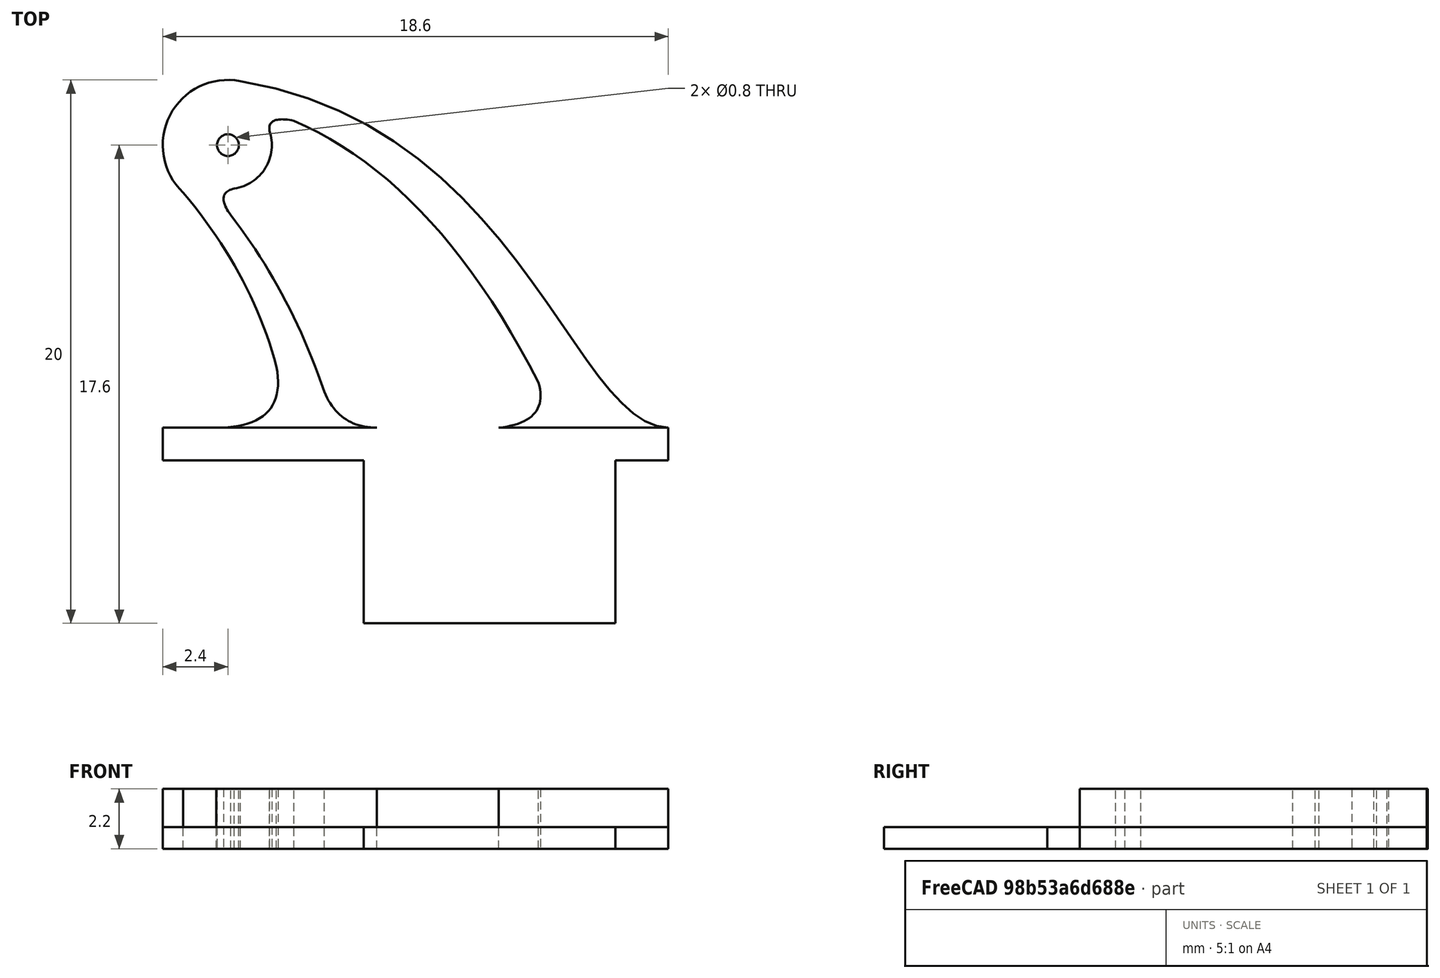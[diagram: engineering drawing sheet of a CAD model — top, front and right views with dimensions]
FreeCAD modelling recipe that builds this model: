
FCSTD DOCUMENT  (FreeCAD 0.20R0.20.2)
Label: 009
License: All rights reserved
LicenseURL: http://en.wikipedia.org/wiki/All_rights_reserved
objects: Sketcher::SketchObject×3, Part::Extrusion×2
note: 5 computed .brp shape members not serialized (recipe doc carries the construction recipe); baked Part::Feature solids carry a one-line shape summary decoded from their .brp

FEATURE [Sketcher::SketchObject] Sketch  label="main"
  FullyConstrained = true
  sketch-geometry (25):
    g0: LineSegment StartX=12.0586 StartY=-6 StartZ=0 EndX=12.0586 EndY=0 EndZ=0
    g1: LineSegment StartX=2.8 StartY=-6 StartZ=0 EndX=2.8 EndY=0 EndZ=0
    g2: LineSegment StartX=2.8 StartY=-6 StartZ=0 EndX=12.0586 EndY=-6 EndZ=0
    g3: LineSegment StartX=12.0586 StartY=0 StartZ=0 EndX=14 EndY=0 EndZ=0
    g4: LineSegment StartX=2.8 StartY=0 StartZ=0 EndX=0 EndY=0 EndZ=0
    g5: LineSegment StartX=14 StartY=0 StartZ=0 EndX=14 EndY=1.2 EndZ=0
    g6: LineSegment StartX=0 StartY=0 StartZ=0 EndX=-4.6 EndY=0 EndZ=0
    g7: Circle CenterX=-2.2 CenterY=11.6 CenterZ=0 NormalX=0 NormalY=0 NormalZ=1 AngleXU=0 Radius=0.4
    g8-g11: Circle x4 (B-spline internal-alignment scaffolding for g12; pole/knot coordinates omitted)
    g12: BSplineCurve PolesCount=4 KnotsCount=2 Degree=3 IsPeriodic=0
    g13: GeomPoint X=-1.74436 Y=13.9564 Z=0
    g14: GeomPoint X=14 Y=1.2 Z=0
    g15: ArcOfCircle CenterX=-2.2 CenterY=11.6 CenterZ=0 NormalX=0 NormalY=0 NormalZ=1 AngleXU=0 Radius=2.4 StartAngle=1.37979 EndAngle=3.95565
    g16: LineSegment StartX=-2.62672 StartY=1.2 StartZ=0 EndX=-4.6 EndY=1.2 EndZ=0
    g17: LineSegment StartX=-4.6 StartY=0 StartZ=0 EndX=-4.6 EndY=1.2 EndZ=0
    g18: Circle CenterX=-2.62672 CenterY=1.2 CenterZ=0 NormalX=0 NormalY=0 NormalZ=1 AngleXU=0 Radius=1
    g19: Circle CenterX=0 CenterY=1.2 CenterZ=0 NormalX=0 NormalY=0 NormalZ=1 AngleXU=0 Radius=1
    g20: Circle CenterX=-0.413885 CenterY=3.44541 CenterZ=0 NormalX=0 NormalY=0 NormalZ=1 AngleXU=0 Radius=1
    g21: BSplineCurve PolesCount=3 KnotsCount=2 Degree=2 IsPeriodic=0
    g22: GeomPoint X=-2.62672 Y=1.2 Z=0
    g23: GeomPoint X=-0.413885 Y=3.44541 Z=0
    g24: BSplineCurve PolesCount=3 KnotsCount=2 Degree=2 IsPeriodic=0
  constraints (52):
    c: Vertical(g0)
    c: Vertical(g1)
    c: Block(g1)
    c: Block(g0)
    c: Distance(g1) = 6
    c: Coincident(g2,g1)
    c: Horizontal(g2)
    c: Coincident(g0,g2)
    c: Block(g2)
    c: Coincident(g3,g0)
    c: Horizontal(g3)
    c: Coincident(g4,g1)
    c: Horizontal(g4)
    c: Block(g3)
    c: Block(g4)
    c: Coincident(g5,g3)
    c: Vertical(g5)
    c: Distance(g5) = 1.2
    c: Coincident(g6,g4)
    c: Horizontal(g6)
    c: Distance(g6) = 4.6
    c: Block(g7)
    c: Weight(g8) = 1
    c: Equal(g8,g9)
    c: Equal(g8,g10)
    c: Equal(g8,g11)
    c: Coincident(g12,g5)
    c: InternalAlignment(g8-g11 -> g12) x4
    c: InternalAlignment(g13,g12)
    c: InternalAlignment(g14,g12)
    c: Block(g12)
    c: Coincident(g15,g7)
    c: Coincident(g15,g12)
    c: Coincident(g15,g24)
    c: Block(g15)
    c: Horizontal(g16)
    c: Coincident(g17,g6)
    c: Vertical(g17)
    c: Coincident(g17,g16)
    c: Weight(g18) = 1
    c: Equal(g18,g19)
    c: Equal(g18,g20)
    c: InternalAlignment(g18,g21)
    c: InternalAlignment(g19,g21)
    c: InternalAlignment(g20,g21)
    c: InternalAlignment(g22,g21)
    c: InternalAlignment(g23,g21)
    c: Block(g16)
    c: Coincident(g16,g21)
    c: Coincident(g21,g24)
    c: Block(g24)
    c: Block(g21)
FEATURE [Part::Extrusion] Extrude
  Base = -> Sketch
  Dir = (0,0,1)
  DirMode = 2
  FaceMakerClass = Part::FaceMakerBullseye
  LengthFwd = 0.8
  LengthRev = 0
  Solid = true
  Symmetric = false
FEATURE [Sketcher::SketchObject] Sketch001  label="main001"
  FullyConstrained = false
  sketch-geometry (45):
    g0: Circle CenterX=-2.2 CenterY=11.6 CenterZ=0 NormalX=0 NormalY=0 NormalZ=1 AngleXU=0 Radius=0.4
    g1-g4: Circle x4 (B-spline internal-alignment scaffolding for g5; pole/knot coordinates omitted)
    g5: BSplineCurve PolesCount=4 KnotsCount=2 Degree=3 IsPeriodic=0
    g6: GeomPoint X=-1.74436 Y=13.9564 Z=0
    g7: GeomPoint X=14 Y=1.2 Z=0
    g8: ArcOfCircle CenterX=-2.2 CenterY=11.6 CenterZ=0 NormalX=0 NormalY=0 NormalZ=1 AngleXU=0 Radius=2.4 StartAngle=1.37979 EndAngle=3.95565
    g9: Circle CenterX=-2.62672 CenterY=1.2 CenterZ=0 NormalX=0 NormalY=0 NormalZ=1 AngleXU=0 Radius=1
    g10: Circle CenterX=0 CenterY=1.2 CenterZ=0 NormalX=0 NormalY=0 NormalZ=1 AngleXU=0 Radius=1
    g11: Circle CenterX=-0.413885 CenterY=3.44541 CenterZ=0 NormalX=0 NormalY=0 NormalZ=1 AngleXU=0 Radius=1
    g12: BSplineCurve PolesCount=3 KnotsCount=2 Degree=2 IsPeriodic=0
    g13: GeomPoint X=-2.62672 Y=1.2 Z=0
    g14: GeomPoint X=-0.413885 Y=3.44541 Z=0
    g15: BSplineCurve PolesCount=3 KnotsCount=2 Degree=2 IsPeriodic=0
    g16: Circle CenterX=1.34801 CenterY=2.51783 CenterZ=0 NormalX=0 NormalY=0 NormalZ=1 AngleXU=0 Radius=1
    g17: Circle CenterX=1.8831 CenterY=1.2 CenterZ=0 NormalX=0 NormalY=0 NormalZ=1 AngleXU=0 Radius=1
    g18: Circle CenterX=3.28198 CenterY=1.2 CenterZ=0 NormalX=0 NormalY=0 NormalZ=1 AngleXU=0 Radius=1
    g19: BSplineCurve PolesCount=3 KnotsCount=2 Degree=2 IsPeriodic=0
    g20: GeomPoint X=1.34801 Y=2.51783 Z=0
    g21: GeomPoint X=3.28198 Y=1.2 Z=0
    g22: Circle CenterX=9.22372 CenterY=2.86164 CenterZ=0 NormalX=0 NormalY=0 NormalZ=1 AngleXU=0 Radius=1
    g23: Circle CenterX=9.64409 CenterY=1.39848 CenterZ=0 NormalX=0 NormalY=0 NormalZ=1 AngleXU=0 Radius=1
    g24: Circle CenterX=7.76214 CenterY=1.2 CenterZ=0 NormalX=0 NormalY=0 NormalZ=1 AngleXU=0 Radius=1
    g25: BSplineCurve PolesCount=3 KnotsCount=2 Degree=2 IsPeriodic=0
    g26: GeomPoint X=9.22372 Y=2.86164 Z=0
    g27: GeomPoint X=7.76214 Y=1.2 Z=0
    g28: LineSegment StartX=-2.62672 StartY=1.2 StartZ=0 EndX=3.28198 EndY=1.2 EndZ=0
    g29: LineSegment StartX=7.76214 StartY=1.2 StartZ=0 EndX=14 EndY=1.2 EndZ=0
    g30: Circle CenterX=-0.671756 CenterY=12.1251 CenterZ=0 NormalX=0 NormalY=0 NormalZ=1 AngleXU=0 Radius=1
    g31: Circle CenterX=-0.754831 CenterY=12.699 CenterZ=0 NormalX=0 NormalY=0 NormalZ=1 AngleXU=0 Radius=1
    g32: Circle CenterX=0.224587 CenterY=12.4971 CenterZ=0 NormalX=0 NormalY=0 NormalZ=1 AngleXU=0 Radius=1
    g33: BSplineCurve PolesCount=3 KnotsCount=2 Degree=2 IsPeriodic=0
    g34: GeomPoint X=-0.671756 Y=12.1251 Z=0
    g35: GeomPoint X=0.224587 Y=12.4971 Z=0
    g36: Circle CenterX=-2.10085 CenterY=9.02995 CenterZ=0 NormalX=0 NormalY=0 NormalZ=1 AngleXU=0 Radius=1
    g37: Circle CenterX=-2.68572 CenterY=9.84108 CenterZ=0 NormalX=0 NormalY=0 NormalZ=1 AngleXU=0 Radius=1
    g38: Circle CenterX=-1.96262 CenterY=10.0016 CenterZ=0 NormalX=0 NormalY=0 NormalZ=1 AngleXU=0 Radius=1
    g39: BSplineCurve PolesCount=3 KnotsCount=2 Degree=2 IsPeriodic=0
    g40: GeomPoint X=-2.10085 Y=9.02995 Z=0
    g41: GeomPoint X=-1.96262 Y=10.0016 Z=0
    g42: ArcOfCircle CenterX=-2.2 CenterY=11.6 CenterZ=0 NormalX=0 NormalY=0 NormalZ=1 AngleXU=0 Radius=1.61593 StartAngle=4.85982 EndAngle=6.61413
    g43: BSplineCurve PolesCount=3 KnotsCount=2 Degree=2 IsPeriodic=0
    g44: BSplineCurve PolesCount=3 KnotsCount=2 Degree=2 IsPeriodic=0
  constraints (76):
    c: Block(g0)
    c: Weight(g1) = 1
    c: Equal(g1,g2)
    c: Equal(g1,g3)
    c: Equal(g1,g4)
    c: InternalAlignment(g1-g4 -> g5) x4
    c: InternalAlignment(g6,g5)
    c: InternalAlignment(g7,g5)
    c: Block(g5)
    c: Coincident(g8,g0)
    c: Coincident(g8,g5)
    c: Coincident(g8,g15)
    c: Block(g8)
    c: Weight(g9) = 1
    c: Equal(g9,g11)
    c: InternalAlignment(g9,g12)
    c: InternalAlignment(g10,g12)
    c: InternalAlignment(g11,g12)
    c: InternalAlignment(g13,g12)
    c: InternalAlignment(g14,g12)
    c: Coincident(g12,g15)
    c: Block(g15)
    c: Block(g12)
    c: Weight(g16) = 1
    c: Equal(g16,g17)
    c: Equal(g16,g18)
    c: InternalAlignment(g16,g19)
    c: InternalAlignment(g17,g19)
    c: InternalAlignment(g18,g19)
    c: InternalAlignment(g20,g19)
    c: InternalAlignment(g21,g19)
    c: Block(g19)
    c: Weight(g22) = 1
    c: Coincident(g25,g43)
    c: Equal(g22,g23)
    c: Equal(g22,g24)
    c: InternalAlignment(g22,g25)
    c: InternalAlignment(g23,g25)
    c: InternalAlignment(g24,g25)
    c: InternalAlignment(g26,g25)
    c: InternalAlignment(g27,g25)
    c: Block(g25)
    c: Coincident(g28,g19)
    c: Horizontal(g28)
    c: Coincident(g29,g25)
    c: Horizontal(g29)
    c: Weight(g30) = 1
    c: Equal(g30,g31)
    c: Equal(g30,g32)
    c: InternalAlignment(g30,g33)
    c: InternalAlignment(g31,g33)
    c: InternalAlignment(g32,g33)
    c: InternalAlignment(g34,g33)
    c: InternalAlignment(g35,g33)
    c: Weight(g36) = 1
    c: Equal(g36,g37)
    c: Equal(g36,g38)
    c: InternalAlignment(g36,g39)
    c: InternalAlignment(g37,g39)
    c: InternalAlignment(g38,g39)
    c: InternalAlignment(g40,g39)
    c: InternalAlignment(g41,g39)
    c: Coincident(g42,g0)
    c: Coincident(g42,g39)
    c: Coincident(g42,g33)
    c: Block(g42)
    c: PointOnObject(g43,g31)
    c: PointOnObject(g44,g37)
    c: Coincident(g33,g43)
    c: Coincident(g39,g44)
    c: Block(g43)
    c: Block(g44)
    c: Block(g39)
    c: Block(g33)
    c: Block(g29)
    c: Block(g28)
FEATURE [Part::Extrusion] Extrude001
  Base = -> Sketch001
  Dir = (0,0,1)
  DirMode = 2
  FaceMakerClass = Part::FaceMakerBullseye
  LengthFwd = 2.2
  LengthRev = 0
  Solid = true
  Symmetric = false
FEATURE [Sketcher::SketchObject] Sketch002
  FullyConstrained = true
  Placement = pos=(0,0,0) rot=(1,0,0;1.5708rad)
  sketch-geometry (14):
    g0: LineSegment StartX=0 StartY=0 StartZ=0 EndX=18.6 EndY=0 EndZ=0
    g1: LineSegment StartX=0 StartY=0 StartZ=0 EndX=9.3 EndY=0 EndZ=0
    g2-g6: Circle x5 (B-spline internal-alignment scaffolding for g7; pole/knot coordinates omitted)
    g7: BSplineCurve PolesCount=5 KnotsCount=3 Degree=3 IsPeriodic=0
    g8: GeomPoint X=0 Y=0 Z=0
    g9: GeomPoint X=9.3 Y=-13.9926 Z=0
    g10: GeomPoint X=18.6 Y=0 Z=0
    g11: Circle CenterX=5.2 CenterY=-4 CenterZ=0 NormalX=0 NormalY=0 NormalZ=1 AngleXU=0 Radius=2.2
    g12: Circle CenterX=13.4 CenterY=-4 CenterZ=0 NormalX=0 NormalY=0 NormalZ=1 AngleXU=0 Radius=2.2
    g13: Circle CenterX=9.3 CenterY=-9.65 CenterZ=0 NormalX=0 NormalY=0 NormalZ=1 AngleXU=0 Radius=2.65
  constraints (18):
    c: Coincident(g0,g-1)
    c: Horizontal(g0)
    c: Distance(g0) = 18.6
    c: Coincident(g1,g0)
    c: Distance(g1) = 9.3
    c: Horizontal(g1)
    c: Weight(g2) = 1
    c: Coincident(g7,g0)
    c: Equal(g2, g3-g6) x4
    c: Coincident(g7,g0)
    c: InternalAlignment(g2-g6 -> g7) x5
    c: InternalAlignment(g8,g7)
    c: InternalAlignment(g9,g7)
    c: InternalAlignment(g10,g7)
    c: Block(g7)
    c: Block(g11)
    c: Block(g12)
    c: Block(g13)
